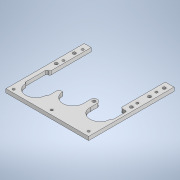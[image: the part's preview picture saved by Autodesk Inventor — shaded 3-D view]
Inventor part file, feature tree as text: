
AUTODESK INVENTOR PART (.ipt)
format: ipt  version: 2021 (Build 250183000, 183)  size: 342,016 bytes
history: native  units: mm
features: sketch x7, extrude x5, hole x2, projected_geometry x1
ambient origin geometry x8: Origin, YZ Plane, XZ Plane, XY Plane, X Axis, Y Axis, Z Axis, Center Point
bodies: Solid1 (feature_tree)
feature tree (15):
  extrude  "Extrusion1"  Depth=112.5mm
  extrude  "Extrusion2"  Depth=5.0mm
  extrude  "Extrusion3"  Depth=27.7mm
  hole  "Hole1"  [1 undecoded]
  hole  "Hole2"  [1 undecoded]
  extrude  "Extrusion4"  Depth=18.5mm
  extrude  "Extrusion5"  Depth=5.0mm TaperAngle=0.0deg
  sketch  "Sketch1"  dims[d0=112.5mm d1=116.5mm]
  sketch  "Sketch2"  dims[d2=5.0mm d3=0.0mm d4=47.7mm]
  sketch  "Sketch3"  dims[d5=27.7mm d6=27.7mm]
  sketch  "Sketch4"  dims[d7=27.7mm d8=27.7mm]
  sketch  "Sketch5"  dims[d9=116.5mm d10=112.5mm]
  projected_geometry  "Projected Loop1"
  sketch  "Sketch6"  dims[d13=37.0mm d14=18.5mm]
  sketch  "Sketch7"  dims[d15=30.9mm d16=5.0mm d17=0.0mm d18=19.5mm d19=35.0mm d20=35.0mm d28=5.0mm d29=0.0mm d48=4.7mm d49=5.5mm d50=4.2mm d51=6.0mm d52=4.0mm d53=2.0mm d54=90.0deg d55=8.0mm d56=20.594885mm d58=30.0mm d59=50.0mm d60=6.0mm d61=6.0mm d62=6.0mm d63=14.0mm d64=40.0mm d65=3.2mm d66=6.0mm d67=4.0mm d68=2.0mm d69=90.0deg d70=8.0mm d71=20.594885mm d72=5.4mm d73=5.4mm d81=2.0mm d82=2.0mm d83=2.0mm d84=2.0mm d86=2.0mm d87=2.0mm d88=27.7mm d89=10.0mm d90=10.0mm d91=25.8mm d92=23.25mm d93=23.25mm d94=37.0mm d95=27.7mm d96=27.7mm d97=19.15mm d98=50.85mm d99=46.75mm d100=2.017mm d101=6.182153mm d102=31.7mm d103=51.7mm d104=30.9mm d105=3.4mm d106=11.9mm d107=61.0mm d108=47.7mm d109=28.0mm d110=18.5mm d111=30.27mm d112=27.7mm d113=2.0mm d114=30.27mm d115=2.0mm d116=112.516739mm d117=116.5mm d120=2.0mm d121=2.0mm d122=2.0mm d123=2.0mm d125=2.0mm d126=2.0mm d127=27.7mm d128=10.0mm d129=10.0mm d130=25.8mm d131=23.25mm d132=23.25mm d133=37.0mm d134=27.7mm d135=27.7mm d136=19.15mm d137=50.85mm d138=46.75mm d139=2.0mm d140=6.182153mm d141=31.7mm d142=51.7mm d143=30.883261mm d144=3.4mm d145=11.9mm d146=61.0mm d147=47.7mm d148=28.0mm d149=18.5mm d150=30.27mm d152=2.0mm d153=30.27mm d154=2.0mm d155=112.5mm d156=116.5mm d157=25.8mm d158=28.0mm d159=10.0mm d160=10.0mm d161=0.0mm d162=58.25mm d163=4.5mm d164=5.4mm d165=2.0mm d166=0.3mm d167=0.0mm]
note: 2 required parameter values undecoded (feature->parameter linkage not recoverable at this tier; creation-order binding heuristic only, values carry confidence <= 0.55)
